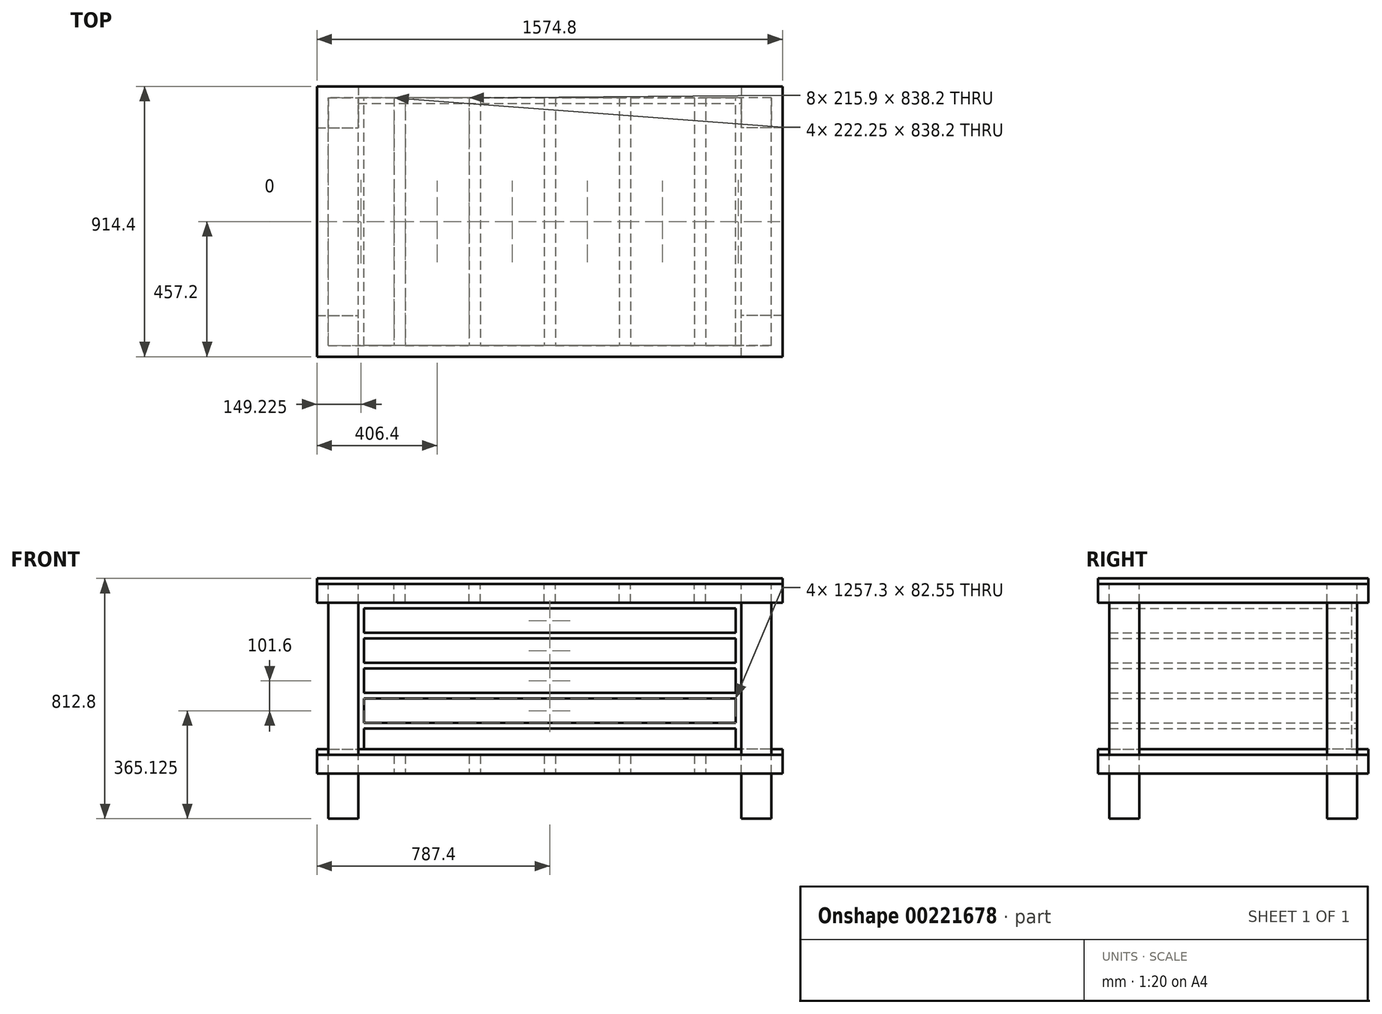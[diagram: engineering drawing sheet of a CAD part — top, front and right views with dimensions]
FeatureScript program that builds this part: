
annotation { "Feature Type Name" : "Feature", "Feature Type Description" : "" }
export const myFeature = defineFeature(function(context is Context, id is Id, definition is map)
    precondition{}
    {
        {
            var Q0;
            Q0=qCreatedBy(makeId("Top.planeOp"),FACE);
            var sketch = newSketch(context, id + "F0", { "sketchPlane" : qUnion([Q0])});
            skLineSegment(sketch, "E0.bottom", {"start": v(0, 0) * mm, "end": v(1574.8, 0) * mm});
            skLineSegment(sketch, "E0.top", {"start": v(0, -914.4) * mm, "end": v(1574.8, -914.4) * mm});
            skLineSegment(sketch, "E0.left", {"start": v(0, 0) * mm, "end": v(0, -914.4) * mm});
            skLineSegment(sketch, "E0.right", {"start": v(1574.8, 0) * mm, "end": v(1574.8, -914.4) * mm});
            skSolve(sketch);
        }
        {
            var Q0;
            Q0=makeQuery(id+"F0.imprint","IMPRINT",FACE,{"disambiguationData":[TD([[makeQuery(id+"F0.imprint","IMPRINT",EDGE,{"derivedFrom":sQuery(id+"F0.wireOp",EDGE,"E0.bottom")}),-1.0]])]});
            extrude(context, id + "F1", {"entities" : qUnion([Q0]), "oppositeDirection" : true, "depth" : 19.05 * mm});
        }
        {
            var Q0;
            Q0=makeQuery(id+"F1.opExtrude","CAP_FACE",FACE,{"disambiguationData":[OSD([sQuery(id+"F0.wireOp",EDGE,"E0.bottom"),sQuery(id+"F0.wireOp",EDGE,"E0.top"),sQuery(id+"F0.wireOp",EDGE,"E0.left"),sQuery(id+"F0.wireOp",EDGE,"E0.right")])],"isStart":false});
            var sketch = newSketch(context, id + "F2", { "sketchPlane" : qUnion([Q0])});
            skLineSegment(sketch, "E1.bottom", {"start": v(0, 914.4) * mm, "end": v(38.1, 914.4) * mm});
            skLineSegment(sketch, "E1.top", {"start": v(0, 0) * mm, "end": v(38.1, 0) * mm});
            skLineSegment(sketch, "E1.left", {"start": v(0, 914.4) * mm, "end": v(0, 0) * mm});
            skLineSegment(sketch, "E1.right", {"start": v(38.1, 914.4) * mm, "end": v(38.1, 0) * mm});
            skLineSegment(sketch, "E2.bottom", {"start": v(1574.8, 914.4) * mm, "end": v(1536.7, 914.4) * mm});
            skLineSegment(sketch, "E2.top", {"start": v(1574.8, 0) * mm, "end": v(1536.7, 0) * mm});
            skLineSegment(sketch, "E2.left", {"start": v(1574.8, 914.4) * mm, "end": v(1574.8, 0) * mm});
            skLineSegment(sketch, "E2.right", {"start": v(1536.7, 914.4) * mm, "end": v(1536.7, 0) * mm});
            skLineSegment(sketch, "E3.bottom", {"start": v(806.45, 38.1) * mm, "end": v(768.35, 38.1) * mm});
            skLineSegment(sketch, "E3.top", {"start": v(806.45, 876.3) * mm, "end": v(768.35, 876.3) * mm});
            skLineSegment(sketch, "E3.left", {"start": v(806.45, 38.1) * mm, "end": v(806.45, 876.3) * mm});
            skLineSegment(sketch, "E3.right", {"start": v(768.35, 38.1) * mm, "end": v(768.35, 876.3) * mm});
            skPoint(sketch, "E3.middle", {"position": v(787.4, 457.2) * mm});
            skLineSegment(sketch, "E4.1.0.0", {"start": v(1060.45, 38.1) * mm, "end": v(1060.45, 876.3) * mm});
            skLineSegment(sketch, "E4.1.0.1", {"start": v(1022.35, 38.1) * mm, "end": v(1022.35, 876.3) * mm});
            skPoint(sketch, "E4.1.0.2", {"position": v(1041.4, 457.2) * mm});
            skLineSegment(sketch, "E4.1.0.3", {"start": v(1060.45, 876.3) * mm, "end": v(1022.35, 876.3) * mm});
            skLineSegment(sketch, "E4.1.0.4", {"start": v(1060.45, 38.1) * mm, "end": v(1022.35, 38.1) * mm});
            skLineSegment(sketch, "E4.2.0.0", {"start": v(1314.45, 38.1) * mm, "end": v(1314.45, 876.3) * mm});
            skLineSegment(sketch, "E4.2.0.1", {"start": v(1276.35, 38.1) * mm, "end": v(1276.35, 876.3) * mm});
            skPoint(sketch, "E4.2.0.2", {"position": v(1295.4, 457.2) * mm});
            skLineSegment(sketch, "E4.2.0.3", {"start": v(1314.45, 876.3) * mm, "end": v(1276.35, 876.3) * mm});
            skLineSegment(sketch, "E4.2.0.4", {"start": v(1314.45, 38.1) * mm, "end": v(1276.35, 38.1) * mm});
            skLineSegment(sketch, "E4.direction1", {"start": v(768.35, 38.1) * mm, "end": v(1022.35, 38.1) * mm, "construction": true});
            skLineSegment(sketch, "E5.1.0.0", {"start": v(514.35, 38.1) * mm, "end": v(514.35, 876.3) * mm});
            skLineSegment(sketch, "E5.1.0.1", {"start": v(552.45, 38.1) * mm, "end": v(552.45, 876.3) * mm});
            skPoint(sketch, "E5.1.0.2", {"position": v(533.4, 457.2) * mm});
            skLineSegment(sketch, "E5.1.0.3", {"start": v(552.45, 38.1) * mm, "end": v(514.35, 38.1) * mm});
            skLineSegment(sketch, "E5.1.0.4", {"start": v(552.45, 876.3) * mm, "end": v(514.35, 876.3) * mm});
            skLineSegment(sketch, "E5.2.0.0", {"start": v(260.35, 38.1) * mm, "end": v(260.35, 876.3) * mm});
            skLineSegment(sketch, "E5.2.0.1", {"start": v(298.45, 38.1) * mm, "end": v(298.45, 876.3) * mm});
            skPoint(sketch, "E5.2.0.2", {"position": v(279.4, 457.2) * mm});
            skLineSegment(sketch, "E5.2.0.3", {"start": v(298.45, 38.1) * mm, "end": v(260.35, 38.1) * mm});
            skLineSegment(sketch, "E5.2.0.4", {"start": v(298.45, 876.3) * mm, "end": v(260.35, 876.3) * mm});
            skLineSegment(sketch, "E5.direction1", {"start": v(768.35, 38.1) * mm, "end": v(514.35, 38.1) * mm, "construction": true});
            skLineSegment(sketch, "E6.bottom", {"start": v(38.1, 914.4) * mm, "end": v(1536.7, 914.4) * mm});
            skLineSegment(sketch, "E6.top", {"start": v(38.1, 876.3) * mm, "end": v(1536.7, 876.3) * mm});
            skLineSegment(sketch, "E6.left", {"start": v(38.1, 914.4) * mm, "end": v(38.1, 876.3) * mm});
            skLineSegment(sketch, "E6.right", {"start": v(1536.7, 914.4) * mm, "end": v(1536.7, 876.3) * mm});
            skLineSegment(sketch, "E7.bottom", {"start": v(1536.7, 0) * mm, "end": v(38.1, 0) * mm});
            skLineSegment(sketch, "E7.top", {"start": v(1536.7, 38.1) * mm, "end": v(38.1, 38.1) * mm});
            skLineSegment(sketch, "E7.left", {"start": v(1536.7, 0) * mm, "end": v(1536.7, 38.1) * mm});
            skLineSegment(sketch, "E7.right", {"start": v(38.1, 0) * mm, "end": v(38.1, 38.1) * mm});
            skSolve(sketch);
        }
        {
            var Q0;
            Q0 = qSketchRegion(id + "F2", true);
            var Q1;
            {var subQ0=sQuery(id+"F2.wireOp",EDGE,"E5.2.0.0");Q1=makeQuery(id+"F2.imprint","IMPRINT",FACE,{"disambiguationData":[TD([[makeQuery(id+"F2.imprint","IMPRINT",EDGE,{"derivedFrom":subQ0}),-1.0]])]});}
            var Q2;
            {var subQ0=sQuery(id+"F2.wireOp",EDGE,"E5.1.0.0");Q2=makeQuery(id+"F2.imprint","IMPRINT",FACE,{"disambiguationData":[TD([[makeQuery(id+"F2.imprint","IMPRINT",EDGE,{"derivedFrom":subQ0}),-1.0]])]});}
            var Q3;
            {var subQ0=sQuery(id+"F2.wireOp",EDGE,"E3.left");Q3=makeQuery(id+"F2.imprint","IMPRINT",FACE,{"disambiguationData":[TD([[makeQuery(id+"F2.imprint","IMPRINT",EDGE,{"derivedFrom":subQ0}),1.0]])]});}
            var Q4;
            {var subQ0=sQuery(id+"F2.wireOp",EDGE,"E4.1.0.0");Q4=makeQuery(id+"F2.imprint","IMPRINT",FACE,{"disambiguationData":[TD([[makeQuery(id+"F2.imprint","IMPRINT",EDGE,{"derivedFrom":subQ0}),1.0]])]});}
            var Q5;
            {var subQ0=sQuery(id+"F2.wireOp",EDGE,"E4.2.0.0");Q5=makeQuery(id+"F2.imprint","IMPRINT",FACE,{"disambiguationData":[TD([[makeQuery(id+"F2.imprint","IMPRINT",EDGE,{"derivedFrom":subQ0}),1.0]])]});}
            extrude(context, id + "F3", {"entities" : qUnion([Q0, Q1, Q2, Q3, Q4, Q5]), "depth" : 63.5 * mm});
        }
        {
            var Q0;
            Q0=makeQuery(id+"F1.opExtrude","CAP_FACE",FACE,{"disambiguationData":[OSD([sQuery(id+"F0.wireOp",EDGE,"E0.bottom"),sQuery(id+"F0.wireOp",EDGE,"E0.top"),sQuery(id+"F0.wireOp",EDGE,"E0.left"),sQuery(id+"F0.wireOp",EDGE,"E0.right")])],"isStart":false});
            var sketch = newSketch(context, id + "F4", { "sketchPlane" : qUnion([Q0])});
            skLineSegment(sketch, "E8.bottom", {"start": v(38.1, 876.3) * mm, "end": v(139.7, 876.3) * mm});
            skLineSegment(sketch, "E8.top", {"start": v(38.1, 774.7) * mm, "end": v(139.7, 774.7) * mm});
            skLineSegment(sketch, "E8.left", {"start": v(38.1, 876.3) * mm, "end": v(38.1, 774.7) * mm});
            skLineSegment(sketch, "E8.right", {"start": v(139.7, 876.3) * mm, "end": v(139.7, 774.7) * mm});
            skLineSegment(sketch, "E9", {"start": v(787.4, 914.4) * mm, "end": v(787.4, 0) * mm});
            skLineSegment(sketch, "E10", {"start": v(0, 457.2) * mm, "end": v(1574.8, 457.2) * mm});
            skLineSegment(sketch, "E11.MirrorCS", {"start": v(1536.7, 876.3) * mm, "end": v(1435.1, 876.3) * mm});
            skLineSegment(sketch, "E12.MirrorCS", {"start": v(1536.7, 774.7) * mm, "end": v(1435.1, 774.7) * mm});
            skLineSegment(sketch, "E13.MirrorCS", {"start": v(1536.7, 876.3) * mm, "end": v(1536.7, 774.7) * mm});
            skLineSegment(sketch, "E14.MirrorCS", {"start": v(1435.1, 876.3) * mm, "end": v(1435.1, 774.7) * mm});
            skLineSegment(sketch, "E15.MirrorCS", {"start": v(1574.8, 457.2) * mm, "end": v(0, 457.2) * mm});
            skLineSegment(sketch, "E16.MirrorCS", {"start": v(1435.1, 38.1) * mm, "end": v(1435.1, 139.7) * mm});
            skLineSegment(sketch, "E17.MirrorCS", {"start": v(1536.7, 38.1) * mm, "end": v(1536.7, 139.7) * mm});
            skLineSegment(sketch, "E18.MirrorCS", {"start": v(1536.7, 139.7) * mm, "end": v(1435.1, 139.7) * mm});
            skLineSegment(sketch, "E19.MirrorCS", {"start": v(1536.7, 38.1) * mm, "end": v(1435.1, 38.1) * mm});
            skLineSegment(sketch, "E20.MirrorCS", {"start": v(38.1, 38.1) * mm, "end": v(139.7, 38.1) * mm});
            skLineSegment(sketch, "E21.MirrorCS", {"start": v(38.1, 139.7) * mm, "end": v(139.7, 139.7) * mm});
            skLineSegment(sketch, "E22.MirrorCS", {"start": v(139.7, 38.1) * mm, "end": v(139.7, 139.7) * mm});
            skLineSegment(sketch, "E23.MirrorCS", {"start": v(38.1, 38.1) * mm, "end": v(38.1, 139.7) * mm});
            skSolve(sketch);
        }
        {
            var Q0;
            Q0=makeQuery(id+"F4.imprint","IMPRINT",FACE,{"disambiguationData":[TD([[makeQuery(id+"F4.imprint","IMPRINT",EDGE,{"derivedFrom":sQuery(id+"F4.wireOp",EDGE,"E8.bottom")}),-1.0]])]});
            var Q1;
            Q1=makeQuery(id+"F4.imprint","IMPRINT",FACE,{"disambiguationData":[TD([[makeQuery(id+"F4.imprint","IMPRINT",EDGE,{"derivedFrom":sQuery(id+"F4.wireOp",EDGE,"E11.MirrorCS")}),1.0]])]});
            var Q2;
            Q2=makeQuery(id+"F4.imprint","IMPRINT",FACE,{"disambiguationData":[TD([[makeQuery(id+"F4.imprint","IMPRINT",EDGE,{"derivedFrom":sQuery(id+"F4.wireOp",EDGE,"E16.MirrorCS")}),-1.0]])]});
            var Q3;
            Q3=makeQuery(id+"F4.imprint","IMPRINT",FACE,{"disambiguationData":[TD([[makeQuery(id+"F4.imprint","IMPRINT",EDGE,{"derivedFrom":sQuery(id+"F4.wireOp",EDGE,"E20.MirrorCS")}),1.0]])]});
            extrude(context, id + "F5", {"entities" : qUnion([Q0, Q1, Q2, Q3]), "depth" : 793.75 * mm});
        }
        {
            var Q0;
            Q0=makeQuery(id+"F5.opExtrude","CAP_FACE",FACE,{"disambiguationData":[OSD([sQuery(id+"F4.wireOp",EDGE,"E11.MirrorCS"),sQuery(id+"F4.wireOp",EDGE,"E12.MirrorCS"),sQuery(id+"F4.wireOp",EDGE,"E13.MirrorCS"),sQuery(id+"F4.wireOp",EDGE,"E14.MirrorCS")])],"isStart":false});
            cPlane(context, id + "F6", {"entities" : qUnion([Q0]), "cplaneType" : CPlaneType.OFFSET, "offset" : 152.4 * mm, "oppositeDirection" : true, "width" : 152.4 * mm, "height" : 152.4 * mm});
        }
        {
            var Q0;
            Q0=qCreatedBy(id+"F6.planeOp",FACE);
            var sketch = newSketch(context, id + "F7", { "sketchPlane" : qUnion([Q0])});
            skLineSegment(sketch, "E24.bottom", {"start": v(0, 914.4) * mm, "end": v(38.1, 914.4) * mm});
            skLineSegment(sketch, "E24.top", {"start": v(0, 0) * mm, "end": v(38.1, 0) * mm});
            skLineSegment(sketch, "E24.left", {"start": v(0, 914.4) * mm, "end": v(0, 0) * mm});
            skLineSegment(sketch, "E24.right", {"start": v(38.1, 914.4) * mm, "end": v(38.1, 0) * mm});
            skLineSegment(sketch, "E25.bottom", {"start": v(1574.8, 914.4) * mm, "end": v(1536.7, 914.4) * mm});
            skLineSegment(sketch, "E25.top", {"start": v(1574.8, 0) * mm, "end": v(1536.7, 0) * mm});
            skLineSegment(sketch, "E25.left", {"start": v(1574.8, 914.4) * mm, "end": v(1574.8, 0) * mm});
            skLineSegment(sketch, "E25.right", {"start": v(1536.7, 914.4) * mm, "end": v(1536.7, 0) * mm});
            skLineSegment(sketch, "E26.bottom", {"start": v(806.45, 38.1) * mm, "end": v(768.35, 38.1) * mm});
            skLineSegment(sketch, "E26.top", {"start": v(806.45, 876.3) * mm, "end": v(768.35, 876.3) * mm});
            skLineSegment(sketch, "E26.left", {"start": v(806.45, 38.1) * mm, "end": v(806.45, 876.3) * mm});
            skLineSegment(sketch, "E26.right", {"start": v(768.35, 38.1) * mm, "end": v(768.35, 876.3) * mm});
            skPoint(sketch, "E26.middle", {"position": v(787.4, 457.2) * mm});
            skLineSegment(sketch, "E27.1.0.0", {"start": v(1060.45, 38.1) * mm, "end": v(1060.45, 876.3) * mm});
            skLineSegment(sketch, "E27.1.0.1", {"start": v(1022.35, 38.1) * mm, "end": v(1022.35, 876.3) * mm});
            skPoint(sketch, "E27.1.0.2", {"position": v(1740.79, 845) * mm});
            skLineSegment(sketch, "E27.1.0.3", {"start": v(1060.45, 876.3) * mm, "end": v(1022.35, 876.3) * mm});
            skLineSegment(sketch, "E27.1.0.4", {"start": v(1060.45, 38.1) * mm, "end": v(1022.35, 38.1) * mm});
            skLineSegment(sketch, "E27.2.0.0", {"start": v(1314.45, 38.1) * mm, "end": v(1314.45, 876.3) * mm});
            skLineSegment(sketch, "E27.2.0.1", {"start": v(1276.35, 38.1) * mm, "end": v(1276.35, 876.3) * mm});
            skPoint(sketch, "E27.2.0.2", {"position": v(1994.79, 845) * mm});
            skLineSegment(sketch, "E27.2.0.3", {"start": v(1314.45, 876.3) * mm, "end": v(1276.35, 876.3) * mm});
            skLineSegment(sketch, "E27.2.0.4", {"start": v(1314.45, 38.1) * mm, "end": v(1276.35, 38.1) * mm});
            skLineSegment(sketch, "E27.direction1", {"start": v(768.35, 38.1) * mm, "end": v(1022.35, 38.1) * mm, "construction": true});
            skLineSegment(sketch, "E28.1.0.0", {"start": v(514.35, 38.1) * mm, "end": v(514.35, 876.3) * mm});
            skLineSegment(sketch, "E28.1.0.1", {"start": v(552.45, 38.1) * mm, "end": v(552.45, 876.3) * mm});
            skPoint(sketch, "E28.1.0.2", {"position": v(533.4, 457.2) * mm});
            skLineSegment(sketch, "E28.1.0.3", {"start": v(552.45, 38.1) * mm, "end": v(514.35, 38.1) * mm});
            skLineSegment(sketch, "E28.1.0.4", {"start": v(552.45, 876.3) * mm, "end": v(514.35, 876.3) * mm});
            skLineSegment(sketch, "E28.2.0.0", {"start": v(260.35, 38.1) * mm, "end": v(260.35, 876.3) * mm});
            skLineSegment(sketch, "E28.2.0.1", {"start": v(298.45, 38.1) * mm, "end": v(298.45, 876.3) * mm});
            skPoint(sketch, "E28.2.0.2", {"position": v(279.4, 457.2) * mm});
            skLineSegment(sketch, "E28.2.0.3", {"start": v(298.45, 38.1) * mm, "end": v(260.35, 38.1) * mm});
            skLineSegment(sketch, "E28.2.0.4", {"start": v(298.45, 876.3) * mm, "end": v(260.35, 876.3) * mm});
            skLineSegment(sketch, "E28.direction1", {"start": v(768.35, 38.1) * mm, "end": v(514.35, 38.1) * mm, "construction": true});
            skLineSegment(sketch, "E29.bottom", {"start": v(38.1, 914.4) * mm, "end": v(1536.7, 914.4) * mm});
            skLineSegment(sketch, "E29.top", {"start": v(38.1, 876.3) * mm, "end": v(1536.7, 876.3) * mm});
            skLineSegment(sketch, "E29.left", {"start": v(38.1, 914.4) * mm, "end": v(38.1, 876.3) * mm});
            skLineSegment(sketch, "E29.right", {"start": v(1536.7, 914.4) * mm, "end": v(1536.7, 876.3) * mm});
            skLineSegment(sketch, "E30.bottom", {"start": v(1536.7, 0) * mm, "end": v(38.1, 0) * mm});
            skLineSegment(sketch, "E30.top", {"start": v(1536.7, 38.1) * mm, "end": v(38.1, 38.1) * mm});
            skLineSegment(sketch, "E30.left", {"start": v(1536.7, 0) * mm, "end": v(1536.7, 38.1) * mm});
            skLineSegment(sketch, "E30.right", {"start": v(38.1, 0) * mm, "end": v(38.1, 38.1) * mm});
            skSolve(sketch);
        }
        {
            var Q0;
            {var subQ0=sQuery(id+"F7.wireOp",EDGE,"E28.1.0.0");Q0=makeQuery(id+"F7.imprint","IMPRINT",FACE,{"disambiguationData":[TD([[makeQuery(id+"F7.imprint","IMPRINT",EDGE,{"derivedFrom":subQ0}),-1.0]])]});}
            var Q1;
            {var subQ0=sQuery(id+"F7.wireOp",EDGE,"E26.left");Q1=makeQuery(id+"F7.imprint","IMPRINT",FACE,{"disambiguationData":[TD([[makeQuery(id+"F7.imprint","IMPRINT",EDGE,{"derivedFrom":subQ0}),1.0]])]});}
            var Q2;
            {var subQ0=sQuery(id+"F7.wireOp",EDGE,"E27.1.0.0");Q2=makeQuery(id+"F7.imprint","IMPRINT",FACE,{"disambiguationData":[TD([[makeQuery(id+"F7.imprint","IMPRINT",EDGE,{"derivedFrom":subQ0}),1.0]])]});}
            var Q3;
            {var subQ0=sQuery(id+"F7.wireOp",EDGE,"E27.2.0.0");Q3=makeQuery(id+"F7.imprint","IMPRINT",FACE,{"disambiguationData":[TD([[makeQuery(id+"F7.imprint","IMPRINT",EDGE,{"derivedFrom":subQ0}),1.0]])]});}
            var Q4;
            Q4=makeQuery(id+"F7.imprint","IMPRINT",FACE,{"disambiguationData":[TD([[makeQuery(id+"F7.imprint","IMPRINT",EDGE,{"derivedFrom":sQuery(id+"F7.wireOp",EDGE,"E25.bottom")}),1.0]])]});
            var Q5;
            Q5=makeQuery(id+"F7.imprint","IMPRINT",FACE,{"disambiguationData":[TD([[makeQuery(id+"F7.imprint","IMPRINT",EDGE,{"derivedFrom":sQuery(id+"F7.wireOp",EDGE,"E30.bottom")}),-1.0]])]});
            var Q6;
            Q6=makeQuery(id+"F7.imprint","IMPRINT",FACE,{"disambiguationData":[TD([[makeQuery(id+"F7.imprint","IMPRINT",EDGE,{"derivedFrom":sQuery(id+"F7.wireOp",EDGE,"E29.bottom")}),-1.0]])]});
            var Q7;
            {var subQ0=sQuery(id+"F7.wireOp",EDGE,"E28.2.0.0");Q7=makeQuery(id+"F7.imprint","IMPRINT",FACE,{"disambiguationData":[TD([[makeQuery(id+"F7.imprint","IMPRINT",EDGE,{"derivedFrom":subQ0}),-1.0]])]});}
            var Q8;
            Q8=makeQuery(id+"F7.imprint","IMPRINT",FACE,{"disambiguationData":[TD([[makeQuery(id+"F7.imprint","IMPRINT",EDGE,{"derivedFrom":sQuery(id+"F7.wireOp",EDGE,"E24.bottom")}),-1.0]])]});
            extrude(context, id + "F8", {"entities" : qUnion([Q0, Q1, Q2, Q3, Q4, Q5, Q6, Q7, Q8]), "oppositeDirection" : true, "depth" : 63.5 * mm});
        }
        {
            var Q0;
            Q0=makeQuery(id+"F8.opExtrude","CAP_FACE",FACE,{"disambiguationData":[OSD([sQuery(id+"F7.wireOp",EDGE,"E24.bottom"),sQuery(id+"F7.wireOp",EDGE,"E24.top"),sQuery(id+"F7.wireOp",EDGE,"E24.left"),sQuery(id+"F7.wireOp",EDGE,"E24.right"),sQuery(id+"F7.wireOp",EDGE,"E25.bottom"),sQuery(id+"F7.wireOp",EDGE,"E25.top"),sQuery(id+"F7.wireOp",EDGE,"E25.left"),sQuery(id+"F7.wireOp",EDGE,"E25.right"),sQuery(id+"F7.wireOp",EDGE,"E26.left"),sQuery(id+"F7.wireOp",EDGE,"E26.right"),sQuery(id+"F7.wireOp",EDGE,"E27.1.0.0"),sQuery(id+"F7.wireOp",EDGE,"E27.1.0.1"),sQuery(id+"F7.wireOp",EDGE,"E27.2.0.0"),sQuery(id+"F7.wireOp",EDGE,"E27.2.0.1"),sQuery(id+"F7.wireOp",EDGE,"E28.1.0.0"),sQuery(id+"F7.wireOp",EDGE,"E28.1.0.1"),sQuery(id+"F7.wireOp",EDGE,"E28.2.0.0"),sQuery(id+"F7.wireOp",EDGE,"E28.2.0.1"),sQuery(id+"F7.wireOp",EDGE,"E29.bottom"),sQuery(id+"F7.wireOp",EDGE,"E29.top"),sQuery(id+"F7.wireOp",EDGE,"E30.bottom"),sQuery(id+"F7.wireOp",EDGE,"E30.top")])],"isStart":false});
            var sketch = newSketch(context, id + "F9", { "sketchPlane" : qUnion([Q0])});
            skSolve(sketch);
        }
        {
            var Q0;
            Q0=makeQuery(id+"F9.imprint","IMPRINT",FACE,{"disambiguationData":[TD([[makeQuery(id+"F9.imprint","IMPRINT",EDGE,{"derivedFrom":makeQuery(id+"F8.opExtrude","CAP_EDGE",EDGE,{"disambiguationData":[OSD([sQuery(id+"F7.wireOp",EDGE,"E24.left")])],"isStart":false})}),-1.0]])]});
            var sketch = newSketch(context, id + "F10", { "sketchPlane" : qUnion([Q0])});
            skLineSegment(sketch, "E31.bottom", {"start": v(0, 0) * mm, "end": v(1435.1, 0) * mm});
            skLineSegment(sketch, "E31.top", {"start": v(139.7, -914.4) * mm, "end": v(1435.1, -914.4) * mm});
            skLineSegment(sketch, "E31.left", {"start": v(0, -139.7) * mm, "end": v(0, -774.7) * mm});
            skLineSegment(sketch, "E31.right", {"start": v(1574.8, -139.7) * mm, "end": v(1574.8, -774.7) * mm});
            skLineSegment(sketch, "E32.top", {"start": v(1574.8, -774.7) * mm, "end": v(1435.1, -774.7) * mm});
            skLineSegment(sketch, "E32.right", {"start": v(1435.1, -914.4) * mm, "end": v(1435.1, -774.7) * mm});
            skLineSegment(sketch, "E33.top", {"start": v(1574.8, -139.7) * mm, "end": v(1435.1, -139.7) * mm});
            skLineSegment(sketch, "E33.right", {"start": v(1435.1, 0) * mm, "end": v(1435.1, -139.7) * mm});
            skLineSegment(sketch, "E34.top", {"start": v(0, -139.7) * mm, "end": v(139.7, -139.7) * mm});
            skLineSegment(sketch, "E34.right", {"start": v(139.7, 0) * mm, "end": v(139.7, -139.7) * mm});
            skLineSegment(sketch, "E35.top", {"start": v(0, -774.7) * mm, "end": v(139.7, -774.7) * mm});
            skLineSegment(sketch, "E35.right", {"start": v(139.7, -914.4) * mm, "end": v(139.7, -774.7) * mm});
            skSolve(sketch);
        }
        {
            var Q0;
            Q0 = qSketchRegion(id + "F10", true);
            extrude(context, id + "F11", {"entities" : qUnion([Q0]), "depth" : 19.05 * mm});
        }
        {
            var Q0;
            Q0=makeQuery(id+"F5.opExtrude","SWEPT_FACE",FACE,{"disambiguationData":[OSD([sQuery(id+"F4.wireOp",EDGE,"E19.MirrorCS")])]});
            cPlane(context, id + "F12", {"entities" : qUnion([Q0]), "cplaneType" : CPlaneType.OFFSET, "offset" : 0 * mm, "width" : 152.4 * mm, "height" : 152.4 * mm});
        }
        {
            var Q0;
            Q0=qCreatedBy(id+"F12.planeOp",FACE);
            var sketch = newSketch(context, id + "F13", { "sketchPlane" : qUnion([Q0])});
            skLineSegment(sketch, "E36.bottom", {"start": v(-1435.1, -82.55) * mm, "end": v(-139.7, -82.55) * mm});
            skLineSegment(sketch, "E36.top", {"start": v(-1435.1, -101.6) * mm, "end": v(-139.7, -101.6) * mm});
            skLineSegment(sketch, "E36.left", {"start": v(-1435.1, -82.55) * mm, "end": v(-1435.1, -101.6) * mm});
            skLineSegment(sketch, "E36.right", {"start": v(-139.7, -82.55) * mm, "end": v(-139.7, -101.6) * mm});
            skLineSegment(sketch, "E37.0.1.0", {"start": v(-1435.1, -184.15) * mm, "end": v(-139.7, -184.15) * mm});
            skLineSegment(sketch, "E37.0.1.1", {"start": v(-1435.1, -203.2) * mm, "end": v(-139.7, -203.2) * mm});
            skLineSegment(sketch, "E37.0.1.2", {"start": v(-139.7, -184.15) * mm, "end": v(-139.7, -203.2) * mm});
            skLineSegment(sketch, "E37.0.1.3", {"start": v(-1435.1, -184.15) * mm, "end": v(-1435.1, -203.2) * mm});
            skLineSegment(sketch, "E37.0.2.0", {"start": v(-1435.1, -285.75) * mm, "end": v(-139.7, -285.75) * mm});
            skLineSegment(sketch, "E37.0.2.1", {"start": v(-1435.1, -304.8) * mm, "end": v(-139.7, -304.8) * mm});
            skLineSegment(sketch, "E37.0.2.2", {"start": v(-139.7, -285.75) * mm, "end": v(-139.7, -304.8) * mm});
            skLineSegment(sketch, "E37.0.2.3", {"start": v(-1435.1, -285.75) * mm, "end": v(-1435.1, -304.8) * mm});
            skLineSegment(sketch, "E37.0.3.0", {"start": v(-1435.1, -387.35) * mm, "end": v(-139.7, -387.35) * mm});
            skLineSegment(sketch, "E37.0.3.1", {"start": v(-1435.1, -406.4) * mm, "end": v(-139.7, -406.4) * mm});
            skLineSegment(sketch, "E37.0.3.2", {"start": v(-139.7, -387.35) * mm, "end": v(-139.7, -406.4) * mm});
            skLineSegment(sketch, "E37.0.3.3", {"start": v(-1435.1, -387.35) * mm, "end": v(-1435.1, -406.4) * mm});
            skLineSegment(sketch, "E37.0.4.0", {"start": v(-1435.1, -488.95) * mm, "end": v(-139.7, -488.95) * mm});
            skLineSegment(sketch, "E37.0.4.1", {"start": v(-1435.1, -508) * mm, "end": v(-139.7, -508) * mm});
            skLineSegment(sketch, "E37.0.4.2", {"start": v(-139.7, -488.95) * mm, "end": v(-139.7, -508) * mm});
            skLineSegment(sketch, "E37.0.4.3", {"start": v(-1435.1, -488.95) * mm, "end": v(-1435.1, -508) * mm});
            skLineSegment(sketch, "E37.direction1", {"start": v(-1435.1, -101.6) * mm, "end": v(-1416.05, -101.6) * mm, "construction": true});
            skLineSegment(sketch, "E37.direction2", {"start": v(-1435.1, -101.6) * mm, "end": v(-1435.1, -203.2) * mm, "construction": true});
            skLineSegment(sketch, "E38.bottom", {"start": v(-1435.1, -82.55) * mm, "end": v(-1416.05, -82.55) * mm});
            skLineSegment(sketch, "E38.top", {"start": v(-1435.1, -577.85) * mm, "end": v(-1416.05, -577.85) * mm});
            skLineSegment(sketch, "E38.left", {"start": v(-1435.1, -82.55) * mm, "end": v(-1435.1, -577.85) * mm});
            skLineSegment(sketch, "E38.right", {"start": v(-1416.05, -82.55) * mm, "end": v(-1416.05, -577.85) * mm});
            skLineSegment(sketch, "E39.bottom", {"start": v(-139.7, -82.55) * mm, "end": v(-158.75, -82.55) * mm});
            skLineSegment(sketch, "E39.top", {"start": v(-139.7, -577.85) * mm, "end": v(-158.75, -577.85) * mm});
            skLineSegment(sketch, "E39.left", {"start": v(-139.7, -82.55) * mm, "end": v(-139.7, -577.85) * mm});
            skLineSegment(sketch, "E39.right", {"start": v(-158.75, -82.55) * mm, "end": v(-158.75, -577.85) * mm});
            skSolve(sketch);
        }
        {
            var Q0;
            {var subQ0=sQuery(id+"F13.wireOp",EDGE,"E38.right");var subQ1=sQuery(id+"F13.wireOp",EDGE,"E37.0.1.0");var subQ2=makeQuery(id+"F13.imprint","INTERSECT",VERTEX,{"derivedFrom":[subQ1,subQ0]});Q0=makeQuery(id+"F13.imprint","IMPRINT",FACE,{"disambiguationData":[TD([[makeQuery(id+"F13.imprint","IMPRINT",EDGE,{"disambiguationData":[TD([[subQ2,-1.0]])],"derivedFrom":subQ1}),-1.0]])]});}
            var Q1;
            {var subQ0=sQuery(id+"F13.wireOp",EDGE,"E38.right");var subQ1=sQuery(id+"F13.wireOp",EDGE,"E37.0.2.0");var subQ2=makeQuery(id+"F13.imprint","INTERSECT",VERTEX,{"derivedFrom":[subQ1,subQ0]});Q1=makeQuery(id+"F13.imprint","IMPRINT",FACE,{"disambiguationData":[TD([[makeQuery(id+"F13.imprint","IMPRINT",EDGE,{"disambiguationData":[TD([[subQ2,-1.0]])],"derivedFrom":subQ1}),-1.0]])]});}
            var Q2;
            {var subQ0=sQuery(id+"F13.wireOp",EDGE,"E38.right");var subQ1=sQuery(id+"F13.wireOp",EDGE,"E37.0.3.0");var subQ2=makeQuery(id+"F13.imprint","INTERSECT",VERTEX,{"derivedFrom":[subQ1,subQ0]});Q2=makeQuery(id+"F13.imprint","IMPRINT",FACE,{"disambiguationData":[TD([[makeQuery(id+"F13.imprint","IMPRINT",EDGE,{"disambiguationData":[TD([[subQ2,-1.0]])],"derivedFrom":subQ1}),-1.0]])]});}
            var Q3;
            {var subQ0=sQuery(id+"F13.wireOp",EDGE,"E38.right");var subQ1=sQuery(id+"F13.wireOp",EDGE,"E37.0.4.0");var subQ2=makeQuery(id+"F13.imprint","INTERSECT",VERTEX,{"derivedFrom":[subQ1,subQ0]});Q3=makeQuery(id+"F13.imprint","IMPRINT",FACE,{"disambiguationData":[TD([[makeQuery(id+"F13.imprint","IMPRINT",EDGE,{"disambiguationData":[TD([[subQ2,-1.0]])],"derivedFrom":subQ1}),-1.0]])]});}
            var Q4;
            {var subQ0=sQuery(id+"F13.wireOp",EDGE,"E36.bottom");Q4=makeQuery(id+"F13.imprint","IMPRINT",FACE,{"disambiguationData":[TD([[makeQuery(id+"F13.imprint","IMPRINT",EDGE,{"derivedFrom":subQ0}),-1.0]])]});}
            var Q5;
            {var subQ0=sQuery(id+"F13.wireOp",EDGE,"E38.left");var subQ1=sQuery(id+"F13.wireOp",EDGE,"E36.top");var subQ2=makeQuery(id+"F13.imprint","INTERSECT",VERTEX,{"derivedFrom":[subQ1,subQ0]});Q5=makeQuery(id+"F13.imprint","IMPRINT",FACE,{"disambiguationData":[TD([[makeQuery(id+"F13.imprint","IMPRINT",EDGE,{"disambiguationData":[TD([[subQ2,-1.0]])],"derivedFrom":subQ1}),-1.0]])]});}
            var Q6;
            {var subQ5=sQuery(id+"F13.wireOp",EDGE,"E38.bottom");Q6=makeQuery(id+"F13.imprint","IMPRINT",FACE,{"disambiguationData":[TD([[makeQuery(id+"F13.imprint","IMPRINT",EDGE,{"derivedFrom":subQ5}),-1.0]])]});}
            var Q7;
            {var subQ0=sQuery(id+"F13.wireOp",EDGE,"E38.left");var subQ1=sQuery(id+"F13.wireOp",EDGE,"E37.0.1.0");var subQ2=makeQuery(id+"F13.imprint","INTERSECT",VERTEX,{"derivedFrom":[subQ1,subQ0]});Q7=makeQuery(id+"F13.imprint","IMPRINT",FACE,{"disambiguationData":[TD([[makeQuery(id+"F13.imprint","IMPRINT",EDGE,{"disambiguationData":[TD([[subQ2,-1.0]])],"derivedFrom":subQ1}),-1.0]])]});}
            var Q8;
            {var subQ0=sQuery(id+"F13.wireOp",EDGE,"E38.left");var subQ1=sQuery(id+"F13.wireOp",EDGE,"E37.0.1.1");var subQ2=makeQuery(id+"F13.imprint","INTERSECT",VERTEX,{"derivedFrom":[subQ1,subQ0]});Q8=makeQuery(id+"F13.imprint","IMPRINT",FACE,{"disambiguationData":[TD([[makeQuery(id+"F13.imprint","IMPRINT",EDGE,{"disambiguationData":[TD([[subQ2,-1.0]])],"derivedFrom":subQ1}),-1.0]])]});}
            var Q9;
            {var subQ0=sQuery(id+"F13.wireOp",EDGE,"E38.left");var subQ1=sQuery(id+"F13.wireOp",EDGE,"E37.0.2.0");var subQ2=makeQuery(id+"F13.imprint","INTERSECT",VERTEX,{"derivedFrom":[subQ1,subQ0]});Q9=makeQuery(id+"F13.imprint","IMPRINT",FACE,{"disambiguationData":[TD([[makeQuery(id+"F13.imprint","IMPRINT",EDGE,{"disambiguationData":[TD([[subQ2,-1.0]])],"derivedFrom":subQ1}),-1.0]])]});}
            var Q10;
            {var subQ0=sQuery(id+"F13.wireOp",EDGE,"E38.left");var subQ1=sQuery(id+"F13.wireOp",EDGE,"E37.0.2.1");var subQ2=makeQuery(id+"F13.imprint","INTERSECT",VERTEX,{"derivedFrom":[subQ1,subQ0]});Q10=makeQuery(id+"F13.imprint","IMPRINT",FACE,{"disambiguationData":[TD([[makeQuery(id+"F13.imprint","IMPRINT",EDGE,{"disambiguationData":[TD([[subQ2,-1.0]])],"derivedFrom":subQ1}),-1.0]])]});}
            var Q11;
            {var subQ0=sQuery(id+"F13.wireOp",EDGE,"E38.left");var subQ1=sQuery(id+"F13.wireOp",EDGE,"E37.0.3.0");var subQ2=makeQuery(id+"F13.imprint","INTERSECT",VERTEX,{"derivedFrom":[subQ1,subQ0]});Q11=makeQuery(id+"F13.imprint","IMPRINT",FACE,{"disambiguationData":[TD([[makeQuery(id+"F13.imprint","IMPRINT",EDGE,{"disambiguationData":[TD([[subQ2,-1.0]])],"derivedFrom":subQ1}),-1.0]])]});}
            var Q12;
            {var subQ0=sQuery(id+"F13.wireOp",EDGE,"E38.left");var subQ1=sQuery(id+"F13.wireOp",EDGE,"E37.0.3.1");var subQ2=makeQuery(id+"F13.imprint","INTERSECT",VERTEX,{"derivedFrom":[subQ1,subQ0]});Q12=makeQuery(id+"F13.imprint","IMPRINT",FACE,{"disambiguationData":[TD([[makeQuery(id+"F13.imprint","IMPRINT",EDGE,{"disambiguationData":[TD([[subQ2,-1.0]])],"derivedFrom":subQ1}),-1.0]])]});}
            var Q13;
            {var subQ5=sQuery(id+"F13.wireOp",EDGE,"E38.top");Q13=makeQuery(id+"F13.imprint","IMPRINT",FACE,{"disambiguationData":[TD([[makeQuery(id+"F13.imprint","IMPRINT",EDGE,{"derivedFrom":subQ5}),1.0]])]});}
            var Q14;
            {var subQ0=sQuery(id+"F13.wireOp",EDGE,"E38.left");var subQ1=sQuery(id+"F13.wireOp",EDGE,"E37.0.4.0");var subQ2=makeQuery(id+"F13.imprint","INTERSECT",VERTEX,{"derivedFrom":[subQ1,subQ0]});Q14=makeQuery(id+"F13.imprint","IMPRINT",FACE,{"disambiguationData":[TD([[makeQuery(id+"F13.imprint","IMPRINT",EDGE,{"disambiguationData":[TD([[subQ2,-1.0]])],"derivedFrom":subQ1}),-1.0]])]});}
            var Q15;
            {var subQ5=sQuery(id+"F13.wireOp",EDGE,"E39.top");Q15=makeQuery(id+"F13.imprint","IMPRINT",FACE,{"disambiguationData":[TD([[makeQuery(id+"F13.imprint","IMPRINT",EDGE,{"derivedFrom":subQ5}),-1.0]])]});}
            var Q16;
            {var subQ0=sQuery(id+"F13.wireOp",EDGE,"E39.left");var subQ1=sQuery(id+"F13.wireOp",EDGE,"E37.0.3.1");var subQ2=makeQuery(id+"F13.imprint","INTERSECT",VERTEX,{"derivedFrom":[subQ1,subQ0]});Q16=makeQuery(id+"F13.imprint","IMPRINT",FACE,{"disambiguationData":[TD([[makeQuery(id+"F13.imprint","IMPRINT",EDGE,{"disambiguationData":[TD([[subQ2,1.0]])],"derivedFrom":subQ1}),-1.0]])]});}
            var Q17;
            {var subQ0=sQuery(id+"F13.wireOp",EDGE,"E39.left");var subQ1=sQuery(id+"F13.wireOp",EDGE,"E37.0.2.1");var subQ2=makeQuery(id+"F13.imprint","INTERSECT",VERTEX,{"derivedFrom":[subQ1,subQ0]});Q17=makeQuery(id+"F13.imprint","IMPRINT",FACE,{"disambiguationData":[TD([[makeQuery(id+"F13.imprint","IMPRINT",EDGE,{"disambiguationData":[TD([[subQ2,1.0]])],"derivedFrom":subQ1}),-1.0]])]});}
            var Q18;
            {var subQ0=sQuery(id+"F13.wireOp",EDGE,"E39.left");var subQ1=sQuery(id+"F13.wireOp",EDGE,"E37.0.4.0");var subQ2=makeQuery(id+"F13.imprint","INTERSECT",VERTEX,{"derivedFrom":[subQ1,subQ0]});Q18=makeQuery(id+"F13.imprint","IMPRINT",FACE,{"disambiguationData":[TD([[makeQuery(id+"F13.imprint","IMPRINT",EDGE,{"disambiguationData":[TD([[subQ2,1.0]])],"derivedFrom":subQ1}),-1.0]])]});}
            var Q19;
            {var subQ0=sQuery(id+"F13.wireOp",EDGE,"E39.left");var subQ1=sQuery(id+"F13.wireOp",EDGE,"E37.0.3.0");var subQ2=makeQuery(id+"F13.imprint","INTERSECT",VERTEX,{"derivedFrom":[subQ1,subQ0]});Q19=makeQuery(id+"F13.imprint","IMPRINT",FACE,{"disambiguationData":[TD([[makeQuery(id+"F13.imprint","IMPRINT",EDGE,{"disambiguationData":[TD([[subQ2,1.0]])],"derivedFrom":subQ1}),-1.0]])]});}
            var Q20;
            {var subQ0=sQuery(id+"F13.wireOp",EDGE,"E39.left");var subQ1=sQuery(id+"F13.wireOp",EDGE,"E37.0.2.0");var subQ2=makeQuery(id+"F13.imprint","INTERSECT",VERTEX,{"derivedFrom":[subQ1,subQ0]});Q20=makeQuery(id+"F13.imprint","IMPRINT",FACE,{"disambiguationData":[TD([[makeQuery(id+"F13.imprint","IMPRINT",EDGE,{"disambiguationData":[TD([[subQ2,1.0]])],"derivedFrom":subQ1}),-1.0]])]});}
            var Q21;
            {var subQ0=sQuery(id+"F13.wireOp",EDGE,"E39.left");var subQ1=sQuery(id+"F13.wireOp",EDGE,"E37.0.1.1");var subQ2=makeQuery(id+"F13.imprint","INTERSECT",VERTEX,{"derivedFrom":[subQ1,subQ0]});Q21=makeQuery(id+"F13.imprint","IMPRINT",FACE,{"disambiguationData":[TD([[makeQuery(id+"F13.imprint","IMPRINT",EDGE,{"disambiguationData":[TD([[subQ2,1.0]])],"derivedFrom":subQ1}),-1.0]])]});}
            var Q22;
            {var subQ0=sQuery(id+"F13.wireOp",EDGE,"E39.left");var subQ1=sQuery(id+"F13.wireOp",EDGE,"E37.0.1.0");var subQ2=makeQuery(id+"F13.imprint","INTERSECT",VERTEX,{"derivedFrom":[subQ1,subQ0]});Q22=makeQuery(id+"F13.imprint","IMPRINT",FACE,{"disambiguationData":[TD([[makeQuery(id+"F13.imprint","IMPRINT",EDGE,{"disambiguationData":[TD([[subQ2,1.0]])],"derivedFrom":subQ1}),-1.0]])]});}
            var Q23;
            {var subQ0=sQuery(id+"F13.wireOp",EDGE,"E39.left");var subQ1=sQuery(id+"F13.wireOp",EDGE,"E36.top");var subQ2=makeQuery(id+"F13.imprint","INTERSECT",VERTEX,{"derivedFrom":[subQ1,subQ0]});Q23=makeQuery(id+"F13.imprint","IMPRINT",FACE,{"disambiguationData":[TD([[makeQuery(id+"F13.imprint","IMPRINT",EDGE,{"disambiguationData":[TD([[subQ2,1.0]])],"derivedFrom":subQ1}),-1.0]])]});}
            var Q24;
            {var subQ5=sQuery(id+"F13.wireOp",EDGE,"E39.bottom");Q24=makeQuery(id+"F13.imprint","IMPRINT",FACE,{"disambiguationData":[TD([[makeQuery(id+"F13.imprint","IMPRINT",EDGE,{"derivedFrom":subQ5}),1.0]])]});}
            extrude(context, id + "F14", {"entities" : qUnion([Q0, Q1, Q2, Q3, Q4, Q5, Q6, Q7, Q8, Q9, Q10, Q11, Q12, Q13, Q14, Q15, Q16, Q17, Q18, Q19, Q20, Q21, Q22, Q23, Q24]), "oppositeDirection" : true, "depth" : 838.2 * mm});
        }
        {
            var Q0;
            Q0=makeQuery(id+"F14.opExtrude","CAP_FACE",FACE,{"disambiguationData":[OSD([sQuery(id+"F13.wireOp",EDGE,"E36.bottom"),sQuery(id+"F13.wireOp",EDGE,"E36.top"),sQuery(id+"F13.wireOp",EDGE,"E37.0.1.0"),sQuery(id+"F13.wireOp",EDGE,"E37.0.1.1"),sQuery(id+"F13.wireOp",EDGE,"E37.0.2.0"),sQuery(id+"F13.wireOp",EDGE,"E37.0.2.1"),sQuery(id+"F13.wireOp",EDGE,"E37.0.3.0"),sQuery(id+"F13.wireOp",EDGE,"E37.0.3.1"),sQuery(id+"F13.wireOp",EDGE,"E37.0.4.0"),sQuery(id+"F13.wireOp",EDGE,"E37.0.4.1"),sQuery(id+"F13.wireOp",EDGE,"E38.bottom"),sQuery(id+"F13.wireOp",EDGE,"E38.top"),sQuery(id+"F13.wireOp",EDGE,"E38.left"),sQuery(id+"F13.wireOp",EDGE,"E38.right"),sQuery(id+"F13.wireOp",EDGE,"E39.bottom"),sQuery(id+"F13.wireOp",EDGE,"E39.top"),sQuery(id+"F13.wireOp",EDGE,"E39.left"),sQuery(id+"F13.wireOp",EDGE,"E39.right")])],"isStart":true});
            var sketch = newSketch(context, id + "F15", { "sketchPlane" : qUnion([Q0])});
            skLineSegment(sketch, "E40.bottom", {"start": v(-139.7, -82.55) * mm, "end": v(-1435.1, -82.55) * mm});
            skLineSegment(sketch, "E40.top", {"start": v(-139.7, -577.85) * mm, "end": v(-1435.1, -577.85) * mm});
            skLineSegment(sketch, "E40.left", {"start": v(-139.7, -82.55) * mm, "end": v(-139.7, -577.85) * mm});
            skLineSegment(sketch, "E40.right", {"start": v(-1435.1, -82.55) * mm, "end": v(-1435.1, -577.85) * mm});
            skSolve(sketch);
        }
        {
            var Q0;
            Q0 = qSketchRegion(id + "F15", true);
            extrude(context, id + "F16", {"entities" : qUnion([Q0]), "oppositeDirection" : true, "depth" : 19.05 * mm});
        }
    });
